# Revit family: 18.Воздушная завеса без нагрева PWZ-C на базе вентиляторов WNP
name_source: partatom
category: Оборудование
revit_build: Autodesk Revit 2016 (Build: 20161004_0715(x64)
units: mm (PartAtom-declared; Revit-internal decimal feet)

## family parameters
Всегда вертикально = Да
На основе рабочей плоскости = Нет
Общий = Нет
При загрузке вырезать с полостями = Нет
Размер круглого соединителя = Использовать диаметр
Тип детали = Нормальный
Точка расчета площади = Нет

## types (6) — shared parameters
Единица измерения = шт.
Завод изготовитель = KORF
И1 = 2000 мм
Ключевая пометка = Вентиляция
Материал = Сталь серая
Наименование и тех.хар-ка = Воздушная завеса без нагрева
Напряжение U,В = 3-380
Раздел = ОВ
Ширина щели = 42 мм
х2 = 1000 мм

## per-type parameters (varying)
| type | А | Б | Б1 | Высота | И2 | Мощность двигателя N,Вт | Сила тока J, А | Тип, марка, обозначение | Ширина | х |
| 60-30 | 600 мм | 300 мм | 90 мм | 300 мм | 750 мм | 1100 | 2.51 | PWZ-C 60-30 H | 600 мм | 525 мм |
| 60-35 | 600 мм | 350 мм | 105 мм | 350 мм | 750 мм | 1500 | 3,45 | PWZ-C 60-35 H | 600 мм | 525 мм |
| 70-40 M | 700 мм | 400 мм | 120 мм | 400 мм | 850 мм | 1500 | 3,45 | PWZ-C 70-40 M H | 700 мм | 595 мм |
| 70-40 | 700 мм | 400 мм | 120 мм | 400 мм | 850 мм | 3 | 5.9 | PWZ-C 70-40 H | 700 мм | 595 мм |
| 80-50 | 800 мм | 500 мм | 150 мм | 500 мм | 975 мм | 3000 | 5.9 | PWZ-C 80-50 H | 800 мм | 683 мм |
| 90-50 | 900 мм | 500 мм | 150 мм | 500 мм | 990 мм | 5500 | 10.7 | PWZ-C 90-50 H | 900 мм | 693 мм |
